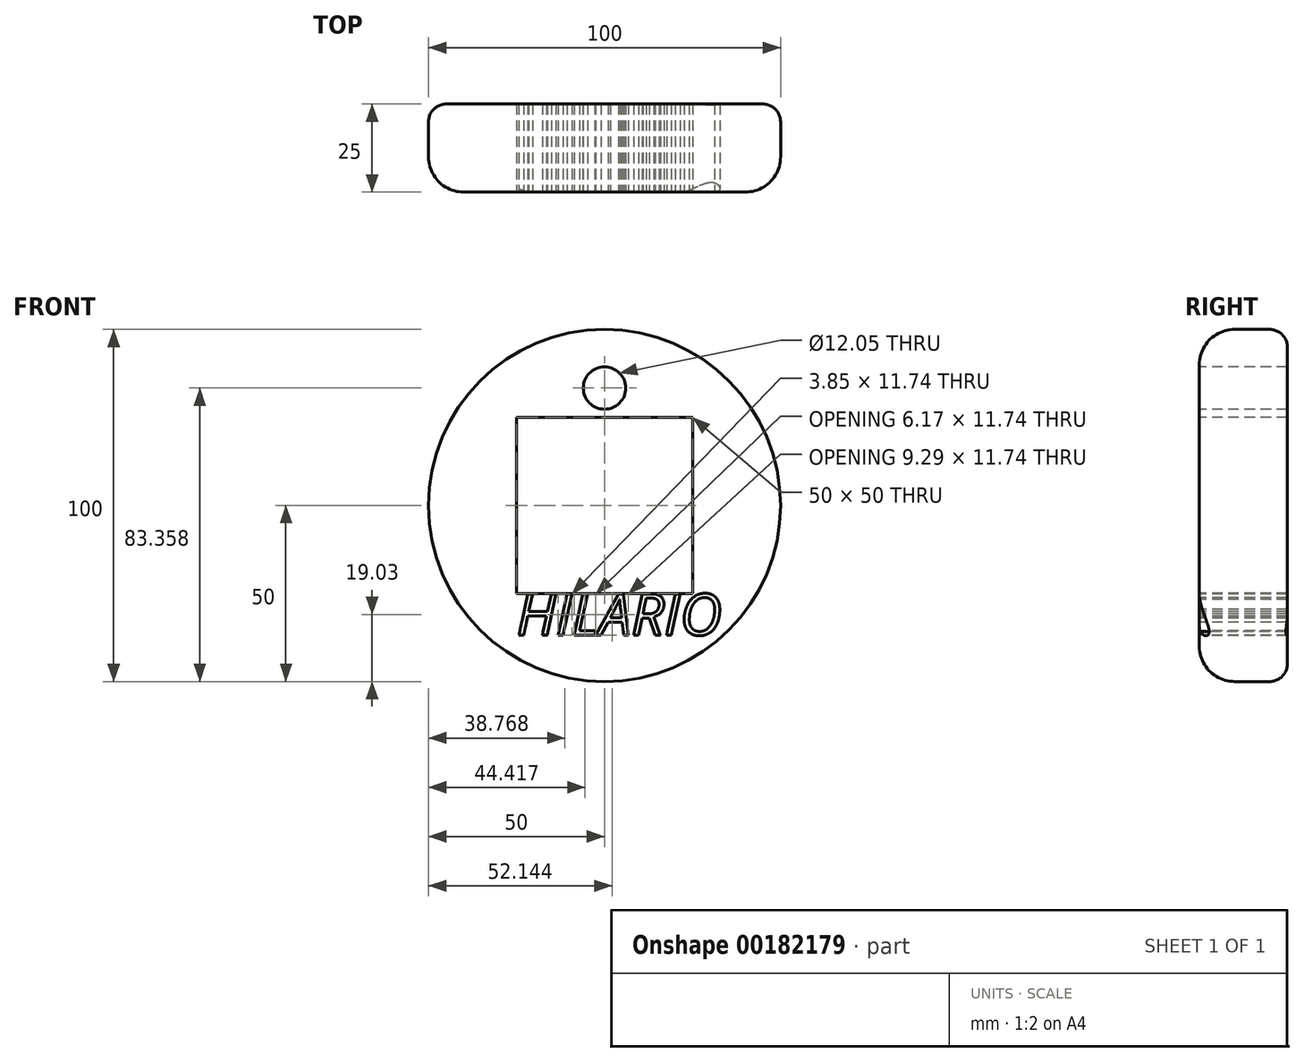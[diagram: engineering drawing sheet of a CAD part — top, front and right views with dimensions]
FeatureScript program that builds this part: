
annotation { "Feature Type Name" : "Feature", "Feature Type Description" : "" }
export const myFeature = defineFeature(function(context is Context, id is Id, definition is map)
    precondition{}
    {
        {
            var Q0;
            Q0=qCreatedBy(makeId("Front.planeOp"),FACE);
            var sketch = newSketch(context, id + "F0", { "sketchPlane" : qUnion([Q0])});
            skCircle(sketch, "E0", {"center": v(0, 0) * mm, "radius": 50 * mm});
            skSolve(sketch);
        }
        {
            var Q0;
            Q0 = qSketchRegion(id + "F0", true);
            extrude(context, id + "F1", {"entities" : qUnion([Q0]), "oppositeDirection" : true, "depth" : 25 * mm});
        }
        {
            var Q0;
            Q0=qCreatedBy(makeId("Front.planeOp"),FACE);
            var sketch = newSketch(context, id + "F2", { "sketchPlane" : qUnion([Q0])});
            skLineSegment(sketch, "E1.bottom", {"start": v(25, -25) * mm, "end": v(-25, -25) * mm});
            skLineSegment(sketch, "E1.top", {"start": v(25, 25) * mm, "end": v(-25, 25) * mm});
            skLineSegment(sketch, "E1.left", {"start": v(25, -25) * mm, "end": v(25, 25) * mm});
            skLineSegment(sketch, "E1.right", {"start": v(-25, -25) * mm, "end": v(-25, 25) * mm});
            skPoint(sketch, "E1.middle", {"position": v(0, 0) * mm});
            skSolve(sketch);
        }
        {
            var Q0;
            Q0=makeQuery(id+"F2.imprint","IMPRINT",FACE,{"disambiguationData":[TD([[makeQuery(id+"F2.imprint","IMPRINT",EDGE,{"derivedFrom":sQuery(id+"F2.wireOp",EDGE,"E1.bottom")}),-1.0]])]});
            extrude(context, id + "F3", {"entities" : qUnion([Q0]), "operationType" : NewBodyOperationType.REMOVE, "oppositeDirection" : true, "depth" : 26 * mm});
        }
        {
            var Q0;
            Q0=makeQuery(id+"F1.opExtrude","CAP_FACE",FACE,{"disambiguationData":[OSD([sQuery(id+"F0.wireOp",EDGE,"E0")])],"isStart":true});
            var sketch = newSketch(context, id + "F4", { "sketchPlane" : qUnion([Q0])});
            skText(sketch, "E2", { "text": "HILARIO\n", "fontName": "OpenSans-Italic.ttf"});
            const initialGuessF4  = {"E2": [-0.025, -0.03684, 1, 0, 0.01184]};
            skSetInitialGuess(sketch, initialGuessF4);
            skSolve(sketch);
        }
        {
            var Q0;
            Q0 = qSketchRegion(id + "F4", true);
            extrude(context, id + "F5", {"entities" : qUnion([Q0]), "operationType" : NewBodyOperationType.REMOVE, "oppositeDirection" : true, "depth" : 25 * mm});
        }
        {
            var Q0;
            Q0=makeQuery(id+"F1.opExtrude","CAP_EDGE",EDGE,{"disambiguationData":[OSD([sQuery(id+"F0.wireOp",EDGE,"E0")])],"isStart":true});
            fillet(context, id + "F6", {"entities" : qUnion([Q0]), "radius" : 10 * mm, "tangentPropagation" : true, "allowEdgeOverflow" : false});
        }
        {
            var Q0;
            Q0=makeQuery(id+"F1.opExtrude","CAP_EDGE",EDGE,{"disambiguationData":[OSD([sQuery(id+"F0.wireOp",EDGE,"E0")])],"isStart":false});
            fillet(context, id + "F7", {"entities" : qUnion([Q0]), "radius" : 5 * mm, "tangentPropagation" : true, "allowEdgeOverflow" : false});
        }
        {
            var Q0;
            {var subQ0=sQuery(id+"F0.wireOp",EDGE,"E0");Q0=makeQuery(id+"F6.opFillet","SPLIT",FACE,{"disambiguationData":[OD(1.0)],"derivedFrom":makeQuery(id+"F5.boolean.opBoolean","SPLIT",FACE,{"disambiguationData":[TD([makeQuery(id+"F1.opExtrude","SWEPT_FACE",FACE,{"disambiguationData":[OSD([subQ0])]})])],"derivedFrom":makeQuery(id+"F1.opExtrude","CAP_FACE",FACE,{"disambiguationData":[OSD([subQ0])],"isStart":true})})});}
            var sketch = newSketch(context, id + "F8", { "sketchPlane" : qUnion([Q0])});
            skCircle(sketch, "E3", {"center": v(0, 33.36) * mm, "radius": 6.03 * mm});
            skSolve(sketch);
        }
        {
            var Q0;
            Q0=makeQuery(id+"F8.imprint","IMPRINT",FACE,{"disambiguationData":[TD([[makeQuery(id+"F8.imprint","IMPRINT",EDGE,{"derivedFrom":sQuery(id+"F8.wireOp",EDGE,"E3")}),1.0]])]});
            extrude(context, id + "F9", {"entities" : qUnion([Q0]), "operationType" : NewBodyOperationType.REMOVE, "oppositeDirection" : true, "depth" : 25 * mm});
        }
    });
